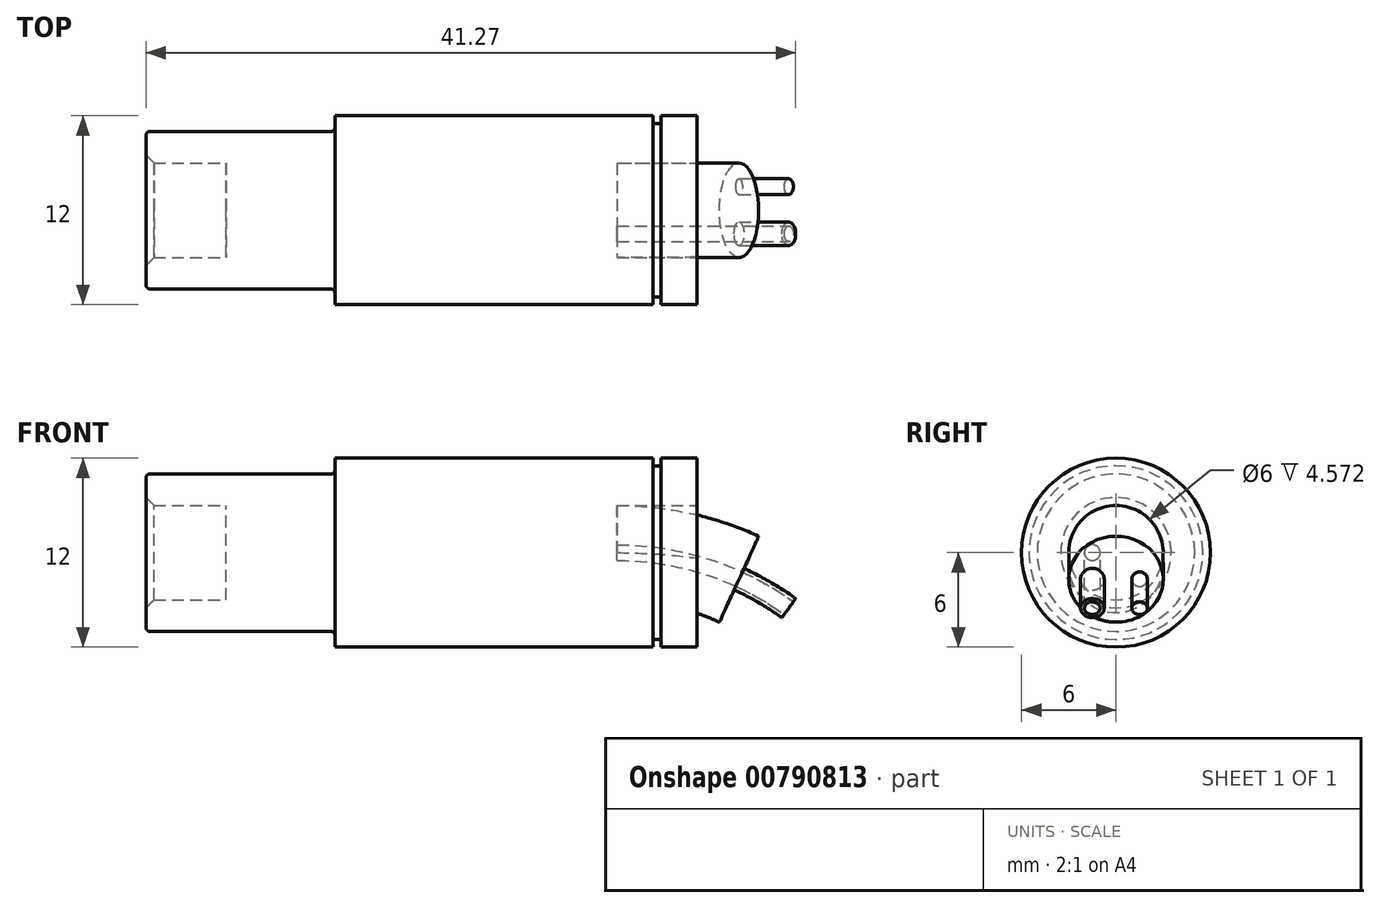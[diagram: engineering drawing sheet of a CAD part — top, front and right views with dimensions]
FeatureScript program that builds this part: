
annotation { "Feature Type Name" : "Feature", "Feature Type Description" : "" }
export const myFeature = defineFeature(function(context is Context, id is Id, definition is map)
    precondition{}
    {
        {
            var Q0;
            Q0=qCreatedBy(makeId("Front.planeOp"),FACE);
            var sketch = newSketch(context, id + "F0", { "sketchPlane" : qUnion([Q0])});
            skLineSegment(sketch, "E0", {"start": v(0, 0) * mm, "end": v(0, 5) * mm});
            skLineSegment(sketch, "E1", {"start": v(0, 5) * mm, "end": v(12, 5) * mm});
            skLineSegment(sketch, "E2", {"start": v(12, 5) * mm, "end": v(12, 6) * mm});
            skLineSegment(sketch, "E3", {"start": v(12, 6) * mm, "end": v(35, 6) * mm});
            skLineSegment(sketch, "E4", {"start": v(35, 6) * mm, "end": v(35, 3) * mm});
            skLineSegment(sketch, "E5", {"start": v(35, 0) * mm, "end": v(0, 0) * mm});
            skLineSegment(sketch, "E6", {"start": v(0, 3) * mm, "end": v(5.08, 3) * mm});
            skLineSegment(sketch, "E7", {"start": v(5.08, 3) * mm, "end": v(5.08, 0) * mm});
            skLineSegment(sketch, "E8", {"start": v(29.92, 3) * mm, "end": v(35, 3) * mm});
            skLineSegment(sketch, "E9", {"start": v(29.92, 3) * mm, "end": v(29.92, 0) * mm});
            skSolve(sketch);
        }
        {
            var Q0;
            {var subQ0=sQuery(id+"F0.wireOp",EDGE,"E1");Q0=makeQuery(id+"F0.imprint","IMPRINT",FACE,{"disambiguationData":[TD([[makeQuery(id+"F0.imprint","IMPRINT",EDGE,{"derivedFrom":subQ0}),-1.0]])]});}
            var Q1;
            Q1=sQuery(id+"F0.wireOp",EDGE,"E5");
            revolve(context, id + "F1", {"surfaceOperationType" : NewSurfaceOperationType.NEW, "entities" : qUnion([Q0]), "axis" : qUnion([Q1]), "revolveType" : RevolveType.FULL});
        }
        {
            var Q0;
            Q0=makeQuery(id+"F1.opRevolve","SWEPT_FACE",FACE,{"disambiguationData":[OSD([sQuery(id+"F0.wireOp",EDGE,"E9")])]});
            var sketch = newSketch(context, id + "F2", { "sketchPlane" : qUnion([Q0])});
            skLineSegment(sketch, "E10", {"start": v(0, 0) * mm, "end": v(1.5, 0) * mm});
            skCircle(sketch, "E11", {"center": v(1.5, 0) * mm, "radius": 0.75 * mm});
            skCircle(sketch, "E12", {"center": v(1.5, 0) * mm, "radius": 0.5 * mm});
            skCircle(sketch, "E13.MirrorC", {"center": v(-1.5, 0) * mm, "radius": 0.75 * mm});
            skCircle(sketch, "E14.MirrorC", {"center": v(-1.5, 0) * mm, "radius": 0.5 * mm});
            skSolve(sketch);
        }
        {
            var Q0;
            Q0=qCreatedBy(makeId("Front.planeOp"),FACE);
            var sketch = newSketch(context, id + "F3", { "sketchPlane" : qUnion([Q0])});
            skArc(sketch, "E15", {"start": v(37.67, -1.68) * mm, "mid": v(33.89, -0.43) * mm, "end": v(29.92, 0) * mm});
            skLineSegment(sketch, "E16", {"start": v(29.92, 0) * mm, "end": v(16.04, 0) * mm});
            skLineSegment(sketch, "E17", {"start": v(29.92, 0) * mm, "end": v(29.92, 0) * mm});
            skArc(sketch, "E18", {"start": v(29.92, 0) * mm, "mid": v(35.65, -0.9) * mm, "end": v(40.83, -3.52) * mm});
            skSolve(sketch);
        }
        {
            var Q0;
            Q0=makeQuery(id+"F2.imprint","IMPRINT",FACE,{"disambiguationData":[TD([[makeQuery(id+"F2.imprint","IMPRINT",EDGE,{"derivedFrom":sQuery(id+"F2.wireOp",EDGE,"E12")}),1.0]])]});
            var Q1;
            Q1=makeQuery(id+"F2.imprint","IMPRINT",FACE,{"disambiguationData":[TD([[makeQuery(id+"F2.imprint","IMPRINT",EDGE,{"derivedFrom":sQuery(id+"F2.wireOp",EDGE,"E11")}),1.0]])]});
            var Q2;
            Q2=makeQuery(id+"F2.imprint","IMPRINT",FACE,{"disambiguationData":[TD([[makeQuery(id+"F2.imprint","IMPRINT",EDGE,{"derivedFrom":sQuery(id+"F2.wireOp",EDGE,"E14.MirrorC")}),-1.0]])]});
            var Q3;
            Q3=makeQuery(id+"F2.imprint","IMPRINT",FACE,{"disambiguationData":[TD([[makeQuery(id+"F2.imprint","IMPRINT",EDGE,{"derivedFrom":sQuery(id+"F2.wireOp",EDGE,"E13.MirrorC")}),-1.0]])]});
            var Q4;
            Q4=sQuery(id+"F3.wireOp",EDGE,"E15");
            sweep(context, id + "F4", {"operationType" : NewBodyOperationType.ADD, "profiles" : qUnion([Q0, Q1, Q2, Q3]), "path" : qUnion([Q4])});
        }
        {
            var Q0;
            Q0=makeQuery(id+"F2.imprint","IMPRINT",FACE,{"disambiguationData":[TD([[makeQuery(id+"F2.imprint","IMPRINT",EDGE,{"derivedFrom":sQuery(id+"F2.wireOp",EDGE,"E14.MirrorC")}),-1.0]])]});
            var Q1;
            Q1=makeQuery(id+"F2.imprint","IMPRINT",FACE,{"disambiguationData":[TD([[makeQuery(id+"F2.imprint","IMPRINT",EDGE,{"derivedFrom":sQuery(id+"F2.wireOp",EDGE,"E12")}),1.0]])]});
            var Q2;
            Q2=sQuery(id+"F3.wireOp",EDGE,"E18");
            sweep(context, id + "F5", {"operationType" : NewBodyOperationType.ADD, "profiles" : qUnion([Q0, Q1]), "path" : qUnion([Q2])});
        }
        {
            var Q0;
            Q0=qCreatedBy(makeId("Top.planeOp"),FACE);
            var sketch = newSketch(context, id + "F6", { "sketchPlane" : qUnion([Q0])});
            skLineSegment(sketch, "E19", {"start": v(32.72, -6.1) * mm, "end": v(32.72, -5.52) * mm});
            skLineSegment(sketch, "E20", {"start": v(32.72, -5.52) * mm, "end": v(32.22, -5.52) * mm});
            skLineSegment(sketch, "E21", {"start": v(32.22, -5.52) * mm, "end": v(32.22, -6.1) * mm});
            skLineSegment(sketch, "E22", {"start": v(32.22, -6.1) * mm, "end": v(32.72, -6.1) * mm});
            skLineSegment(sketch, "E23", {"start": v(34.4, 0) * mm, "end": v(29.88, 0) * mm});
            skSolve(sketch);
        }
        {
            var Q0;
            Q0=makeQuery(id+"F6.imprint","IMPRINT",FACE,{"disambiguationData":[TD([[makeQuery(id+"F6.imprint","IMPRINT",EDGE,{"derivedFrom":sQuery(id+"F6.wireOp",EDGE,"E19")}),1.0]])]});
            var Q1;
            Q1=sQuery(id+"F6.wireOp",EDGE,"E23");
            revolve(context, id + "F7", {"operationType" : NewBodyOperationType.REMOVE, "surfaceOperationType" : NewSurfaceOperationType.NEW, "entities" : qUnion([Q0]), "axis" : qUnion([Q1]), "revolveType" : RevolveType.FULL, "oppositeDirection" : true});
        }
        {
            var Q0;
            Q0=makeQuery(id+"F1.opRevolve","SWEPT_EDGE",EDGE,{"disambiguationData":[OSD([sQuery(id+"F0.wireOp",EDGE,"E1"),sQuery(id+"F0.wireOp",EDGE,"E2")])]});
            fillet(context, id + "F8", {"entities" : qUnion([Q0]), "radius" : 0.25 * mm, "tangentPropagation" : true, "allowEdgeOverflow" : false});
        }
        {
            var Q0;
            Q0=makeQuery(id+"F1.opRevolve","SWEPT_EDGE",EDGE,{"disambiguationData":[OSD([sQuery(id+"F0.wireOp",EDGE,"E0"),sQuery(id+"F0.wireOp",EDGE,"E1")])]});
            fillet(context, id + "F9", {"entities" : qUnion([Q0]), "radius" : 0.25 * mm, "tangentPropagation" : true, "allowEdgeOverflow" : false});
        }
        {
            var Q0;
            Q0=makeQuery(id+"F1.opRevolve","SWEPT_EDGE",EDGE,{"disambiguationData":[OSD([sQuery(id+"F0.wireOp",EDGE,"E0"),sQuery(id+"F0.wireOp",EDGE,"E6")])]});
            chamfer(context, id + "F10", {"entities" : qUnion([Q0]), "width" : 0.5 * mm, "tangentPropagation" : true});
        }
    });
